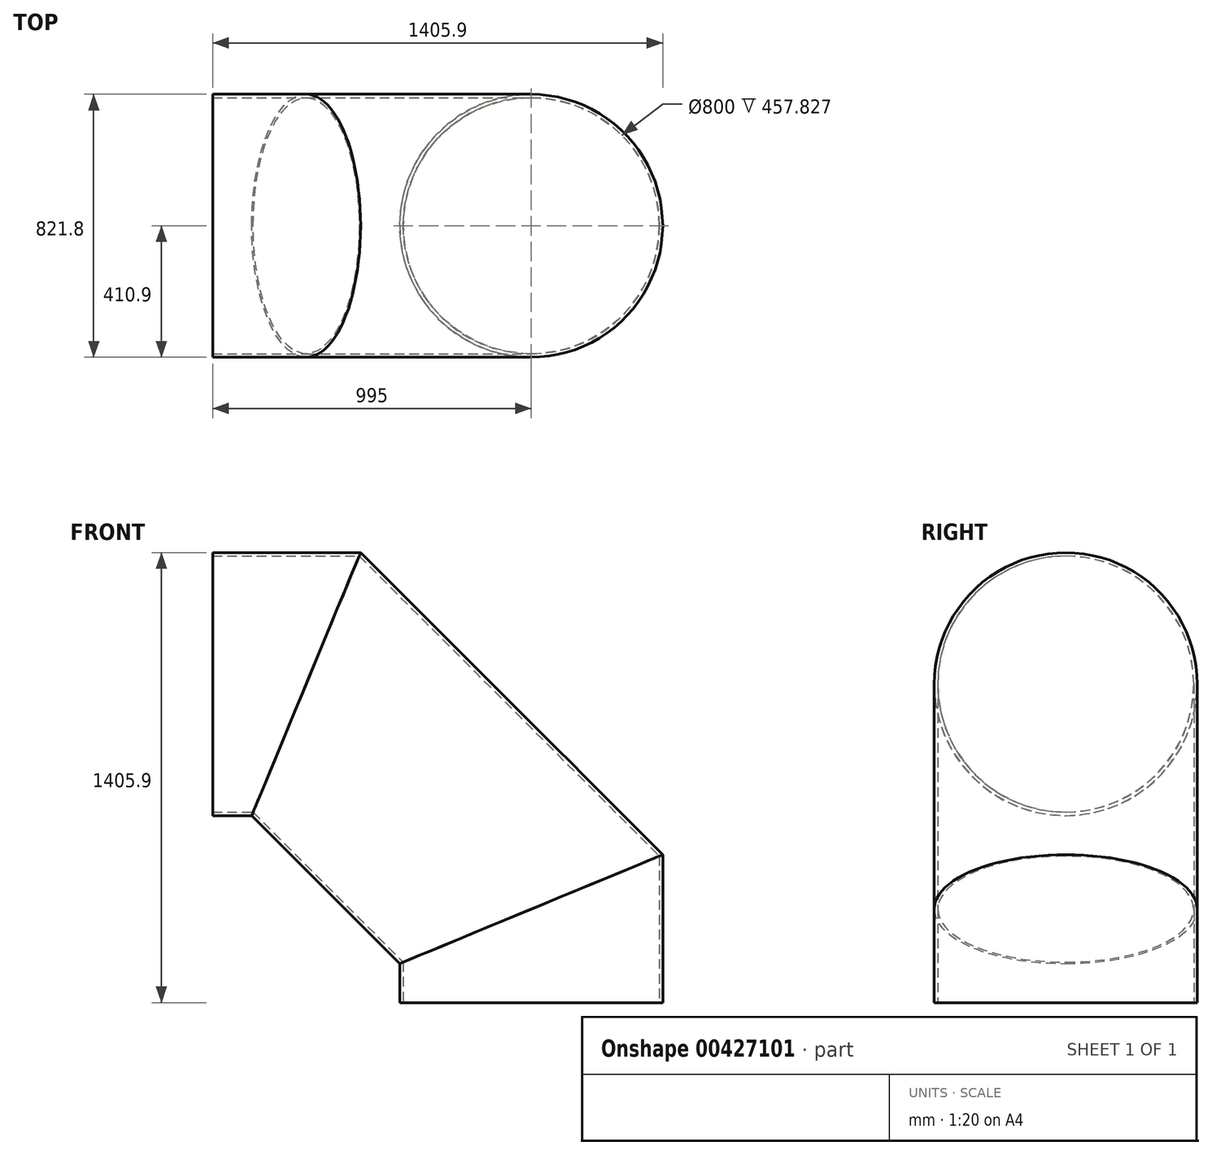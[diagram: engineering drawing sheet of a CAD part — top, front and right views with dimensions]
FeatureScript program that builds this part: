
annotation { "Feature Type Name" : "Feature", "Feature Type Description" : "" }
export const myFeature = defineFeature(function(context is Context, id is Id, definition is map)
    precondition{}
    {
        {
            var Q0;
            Q0=qCreatedBy(makeId("Front.planeOp"),FACE);
            var sketch = newSketch(context, id + "F0", { "sketchPlane" : qUnion([Q0])});
            skLineSegment(sketch, "E0", {"start": v(205, 1200) * mm, "end": v(497.06, 1200) * mm});
            skLineSegment(sketch, "E1", {"start": v(497.06, 1200) * mm, "end": v(1200, 497.06) * mm});
            skLineSegment(sketch, "E2", {"start": v(1200, 205) * mm, "end": v(1200, 497.06) * mm});
            skCircle(sketch, "E3", {"center": v(0, 0) * mm, "radius": 1200 * mm});
            skLineSegment(sketch, "E4", {"start": v(1200, -497.06) * mm, "end": v(789.1, -497.06) * mm});
            skLineSegment(sketch, "E5", {"start": v(789.1, -497.06) * mm, "end": v(789.1, 327) * mm});
            skLineSegment(sketch, "E6", {"start": v(789.1, 327) * mm, "end": v(327, 789.1) * mm});
            skLineSegment(sketch, "E7", {"start": v(327, 789.1) * mm, "end": v(-497.06, 789.1) * mm});
            skLineSegment(sketch, "E8", {"start": v(-497.06, 789.1) * mm, "end": v(-497.06, 1200) * mm});
            skLineSegment(sketch, "E9", {"start": v(-52.6, 0) * mm, "end": v(1200, 0) * mm, "construction": true});
            skLineSegment(sketch, "E10", {"start": v(0, 0) * mm, "end": v(0, 1200) * mm, "construction": true});
            skLineSegment(sketch, "E11", {"start": v(0, 0) * mm, "end": v(848.53, 848.53) * mm, "construction": true});
            skLineSegment(sketch, "E12", {"start": v(789.1, 315) * mm, "end": v(1044.04, 315) * mm, "construction": true});
            skSolve(sketch);
        }
        {
            var Q0;
            Q0=sQuery(id+"F0.wireOp",VERTEX,"E0.start");
            var Q1;
            Q1=sQuery(id+"F0.wireOp",EDGE,"E0");
            cPlane(context, id + "F1", {"entities" : qUnion([Q0, Q1]), "cplaneType" : CPlaneType.LINE_POINT, "offset" : 0 * mm, "oppositeDirection" : true, "width" : 150 * mm, "height" : 150 * mm});
        }
        {
            var Q0;
            Q0=qCreatedBy(id+"F1.planeOp",FACE);
            var sketch = newSketch(context, id + "F2", { "sketchPlane" : qUnion([Q0])});
            skCircle(sketch, "E13", {"center": v(0, 1200) * mm, "radius": 410.9 * mm});
            skCircle(sketch, "E14", {"center": v(0, 1200) * mm, "radius": 400 * mm});
            skSolve(sketch);
        }
        {
            var Q0;
            Q0=makeQuery(id+"F2.imprint","IMPRINT",FACE,{"disambiguationData":[TD([[makeQuery(id+"F2.imprint","IMPRINT",EDGE,{"derivedFrom":sQuery(id+"F2.wireOp",EDGE,"E13")}),1.0]])]});
            var Q1;
            Q1=sQuery(id+"F2.wireOp",EDGE,"E13");
            var Q2;
            Q2=sQuery(id+"F0.wireOp",EDGE,"E0");
            var Q3;
            Q3=sQuery(id+"F0.wireOp",EDGE,"E1");
            var Q4;
            Q4=sQuery(id+"F0.wireOp",EDGE,"E2");
            sweep(context, id + "F3", {"profiles" : qUnion([Q0]), "surfaceProfiles" : qUnion([Q1]), "path" : qUnion([Q2, Q3, Q4])});
        }
    });
